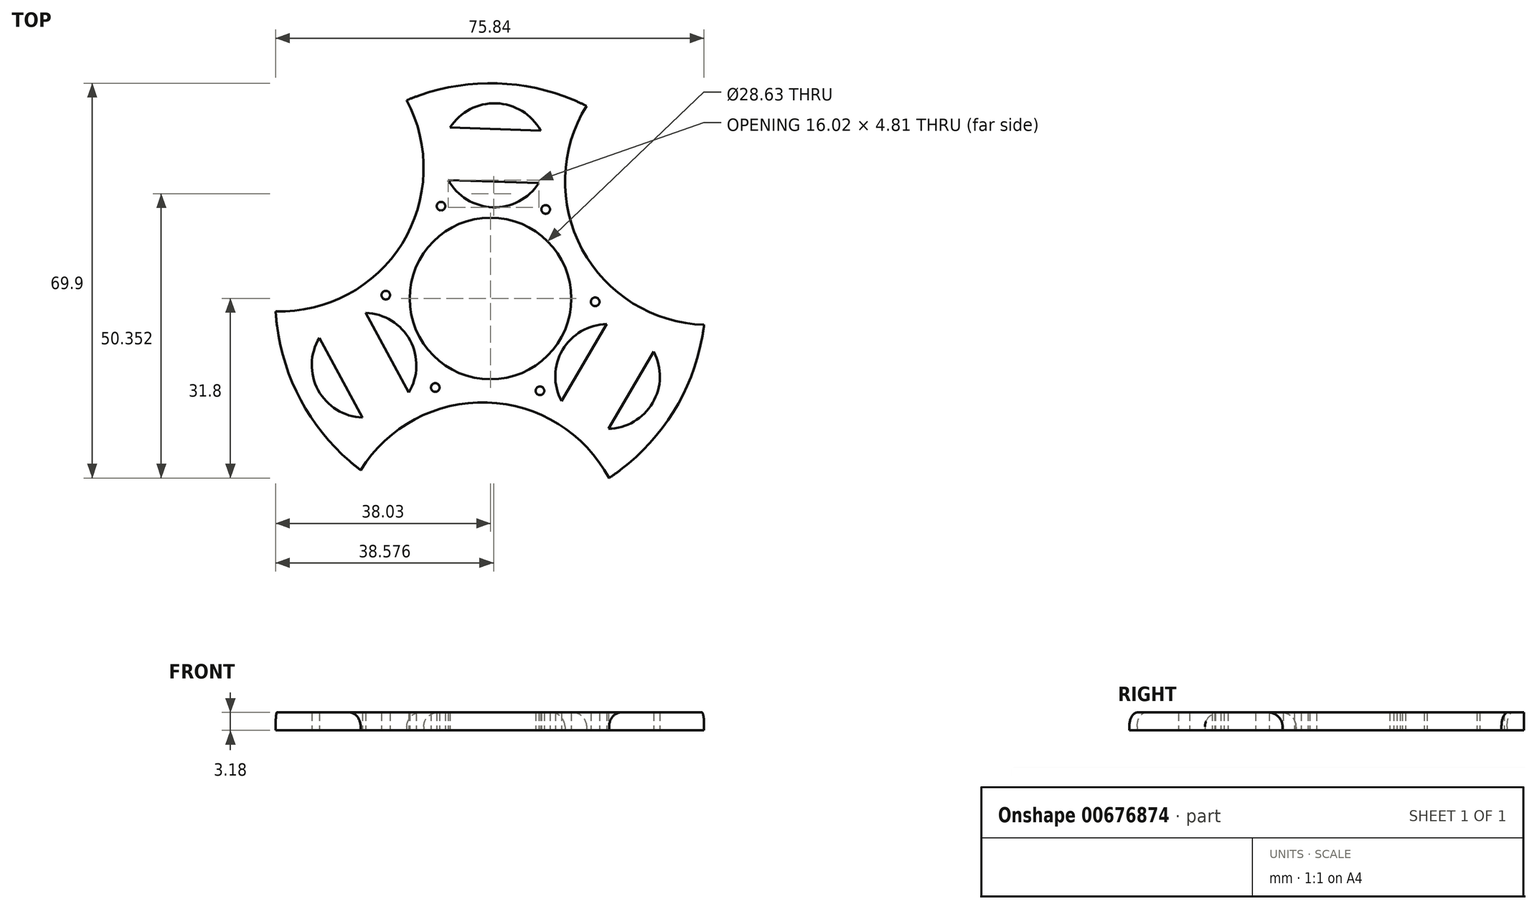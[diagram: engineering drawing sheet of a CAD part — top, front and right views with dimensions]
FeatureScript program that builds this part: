
annotation { "Feature Type Name" : "Feature", "Feature Type Description" : "" }
export const myFeature = defineFeature(function(context is Context, id is Id, definition is map)
    precondition{}
    {
        {
            var Q0;
            Q0=qCreatedBy(makeId("Top.planeOp"),FACE);
            var sketch = newSketch(context, id + "F0", { "sketchPlane" : qUnion([Q0])});
            skCircle(sketch, "E0.cCircle", {"center": v(0, 0) * mm, "radius": 38.1 * mm});
            skPoint(sketch, "E0.0.midPoint", {"position": v(-32.38, 20.08) * mm});
            skLineSegment(sketch, "E1", {"start": v(-43.96, 1.34) * mm, "end": v(20.02, 35.73) * mm, "construction": true});
            skLineSegment(sketch, "E2", {"start": v(21.09, -38.3) * mm, "end": v(20.02, 35.73) * mm, "construction": true});
            skLineSegment(sketch, "E3", {"start": v(21.09, -38.3) * mm, "end": v(-30.3, -6.99) * mm, "construction": true});
            skLineSegment(sketch, "E4", {"start": v(-20.75, 38.8) * mm, "end": v(-22.08, -2.55) * mm, "construction": true});
            skLineSegment(sketch, "E5", {"start": v(43.57, -1.57) * mm, "end": v(-23.2, -37.35) * mm, "construction": true});
            skLineSegment(sketch, "E6", {"start": v(-20.75, 38.8) * mm, "end": v(43.57, -1.57) * mm, "construction": true});
            skCircle(sketch, "E7", {"center": v(0, 0) * mm, "radius": 14.31 * mm});
            skArc(sketch, "E8", {"start": v(-38.03, -2.27) * mm, "mid": v(-15.65, 9.72) * mm, "end": v(-14.83, 35.1) * mm});
            skArc(sketch, "E9", {"start": v(17, 34.1) * mm, "mid": v(16.22, 8.71) * mm, "end": v(37.81, -4.65) * mm});
            skArc(sketch, "E10", {"start": v(21, -31.8) * mm, "mid": v(-0.59, -18.4) * mm, "end": v(-22.97, -30.4) * mm});
            skLineSegment(sketch, "E11", {"start": v(20.6, -4.54) * mm, "end": v(12.56, -18.19) * mm});
            skLineSegment(sketch, "E12", {"start": v(28.9, -9.43) * mm, "end": v(20.87, -23.08) * mm});
            skLineSegment(sketch, "E13", {"start": v(-7.46, 20.96) * mm, "end": v(8.55, 20.42) * mm});
            skLineSegment(sketch, "E14", {"start": v(-7.15, 30.27) * mm, "end": v(8.87, 29.73) * mm});
            skLineSegment(sketch, "E15", {"start": v(-30.3, -6.99) * mm, "end": v(-43.96, 1.34) * mm, "construction": true});
            skLineSegment(sketch, "E16", {"start": v(-30.3, -6.99) * mm, "end": v(-30.3, -6.99) * mm});
            skLineSegment(sketch, "E17", {"start": v(-22.08, -2.55) * mm, "end": v(-22.08, -2.55) * mm});
            skLineSegment(sketch, "E18", {"start": v(-22.08, -2.55) * mm, "end": v(-23.2, -37.35) * mm, "construction": true});
            skArc(sketch, "E19", {"start": v(-30.3, -6.99) * mm, "mid": v(-30.51, -16.21) * mm, "end": v(-22.67, -21.08) * mm});
            skArc(sketch, "E20", {"start": v(-14.46, -16.64) * mm, "mid": v(-14.25, -7.42) * mm, "end": v(-22.08, -2.55) * mm});
            skLineSegment(sketch, "E21", {"start": v(-30.3, -6.99) * mm, "end": v(-22.67, -21.08) * mm});
            skLineSegment(sketch, "E22", {"start": v(-22.08, -2.55) * mm, "end": v(-14.46, -16.64) * mm});
            skArc(sketch, "E23", {"start": v(20.6, -4.54) * mm, "mid": v(12.76, -9.1) * mm, "end": v(12.56, -18.19) * mm});
            skArc(sketch, "E24", {"start": v(20.87, -23.08) * mm, "mid": v(28.7, -18.5) * mm, "end": v(28.9, -9.43) * mm});
            skArc(sketch, "E25", {"start": v(8.87, 29.73) * mm, "mid": v(1.01, 34.56) * mm, "end": v(-7.15, 30.27) * mm});
            skArc(sketch, "E26", {"start": v(-7.46, 20.96) * mm, "mid": v(0.4, 16.15) * mm, "end": v(8.55, 20.42) * mm});
            skCircle(sketch, "E27.cCircle", {"center": v(0, 0) * mm, "radius": 16.06 * mm, "construction": true});
            skPoint(sketch, "E27.0.midPoint", {"position": v(-14.16, -7.59) * mm});
            skCircle(sketch, "E28", {"center": v(-8.76, 16.35) * mm, "radius": 0.76 * mm});
            skCircle(sketch, "E29", {"center": v(9.78, 15.76) * mm, "radius": 0.76 * mm});
            skCircle(sketch, "E30", {"center": v(18.54, -0.59) * mm, "radius": 0.76 * mm});
            skCircle(sketch, "E31", {"center": v(8.76, -16.35) * mm, "radius": 0.76 * mm});
            skCircle(sketch, "E32", {"center": v(-9.78, -15.76) * mm, "radius": 0.76 * mm});
            skCircle(sketch, "E33", {"center": v(-18.54, 0.59) * mm, "radius": 0.76 * mm});
            skSolve(sketch);
        }
        {
            var Q0;
            Q0=makeQuery(id+"F0.imprint","IMPRINT",FACE,{"disambiguationData":[TD([[makeQuery(id+"F0.imprint","IMPRINT",EDGE,{"derivedFrom":sQuery(id+"F0.wireOp",EDGE,"E7")}),-1.0]])]});
            extrude(context, id + "F1", {"entities" : qUnion([Q0]), "depth" : 3.17 * mm, "offsetDistance" : 25.4 * mm});
        }
        {
            var Q0;
            Q0=makeQuery(id+"F1.opExtrude","CAP_EDGE",EDGE,{"disambiguationData":[OSD([sQuery(id+"F0.wireOp",EDGE,"E10")])],"isStart":false});
            var Q1;
            {var subQ0=sQuery(id+"F0.wireOp",EDGE,"E0.cCircle");Q1=makeQuery(id+"F1.opExtrude","CAP_EDGE",EDGE,{"disambiguationData":[OSD([subQ0]),TDD([makeQuery(id+"F0.imprint","IMPRINT",EDGE,{"disambiguationData":[TD([[makeQuery(id+"F0.imprint","INTERSECT",VERTEX,{"disambiguationData":[OD(0.0)],"derivedFrom":[subQ0,sQuery(id+"F0.wireOp",EDGE,"E8")]}),1.0]])],"derivedFrom":subQ0})])],"isStart":false});}
            var Q2;
            Q2=makeQuery(id+"F1.opExtrude","CAP_EDGE",EDGE,{"disambiguationData":[OSD([sQuery(id+"F0.wireOp",EDGE,"E8")])],"isStart":false});
            var Q3;
            {var subQ0=sQuery(id+"F0.wireOp",EDGE,"E0.cCircle");Q3=makeQuery(id+"F1.opExtrude","CAP_EDGE",EDGE,{"disambiguationData":[OSD([subQ0]),TDD([makeQuery(id+"F0.imprint","IMPRINT",EDGE,{"disambiguationData":[TD([[makeQuery(id+"F0.imprint","INTERSECT",VERTEX,{"disambiguationData":[OD(1.0)],"derivedFrom":[subQ0,sQuery(id+"F0.wireOp",EDGE,"E8")]}),-1.0]])],"derivedFrom":subQ0})])],"isStart":false});}
            var Q4;
            Q4=makeQuery(id+"F1.opExtrude","CAP_EDGE",EDGE,{"disambiguationData":[OSD([sQuery(id+"F0.wireOp",EDGE,"E9")])],"isStart":false});
            var Q5;
            {var subQ0=sQuery(id+"F0.wireOp",EDGE,"E0.cCircle");Q5=makeQuery(id+"F1.opExtrude","CAP_EDGE",EDGE,{"disambiguationData":[OSD([subQ0]),TDD([makeQuery(id+"F0.imprint","IMPRINT",EDGE,{"disambiguationData":[TD([[makeQuery(id+"F0.imprint","INTERSECT",VERTEX,{"disambiguationData":[OD(1.0)],"derivedFrom":[subQ0,sQuery(id+"F0.wireOp",EDGE,"E9")]}),-1.0]])],"derivedFrom":subQ0})])],"isStart":false});}
            fillet(context, id + "F2", {"entities" : qUnion([Q0, Q1, Q2, Q3, Q4, Q5]), "radius" : 2.54 * mm, "tangentPropagation" : true, "allowEdgeOverflow" : false});
        }
    });
